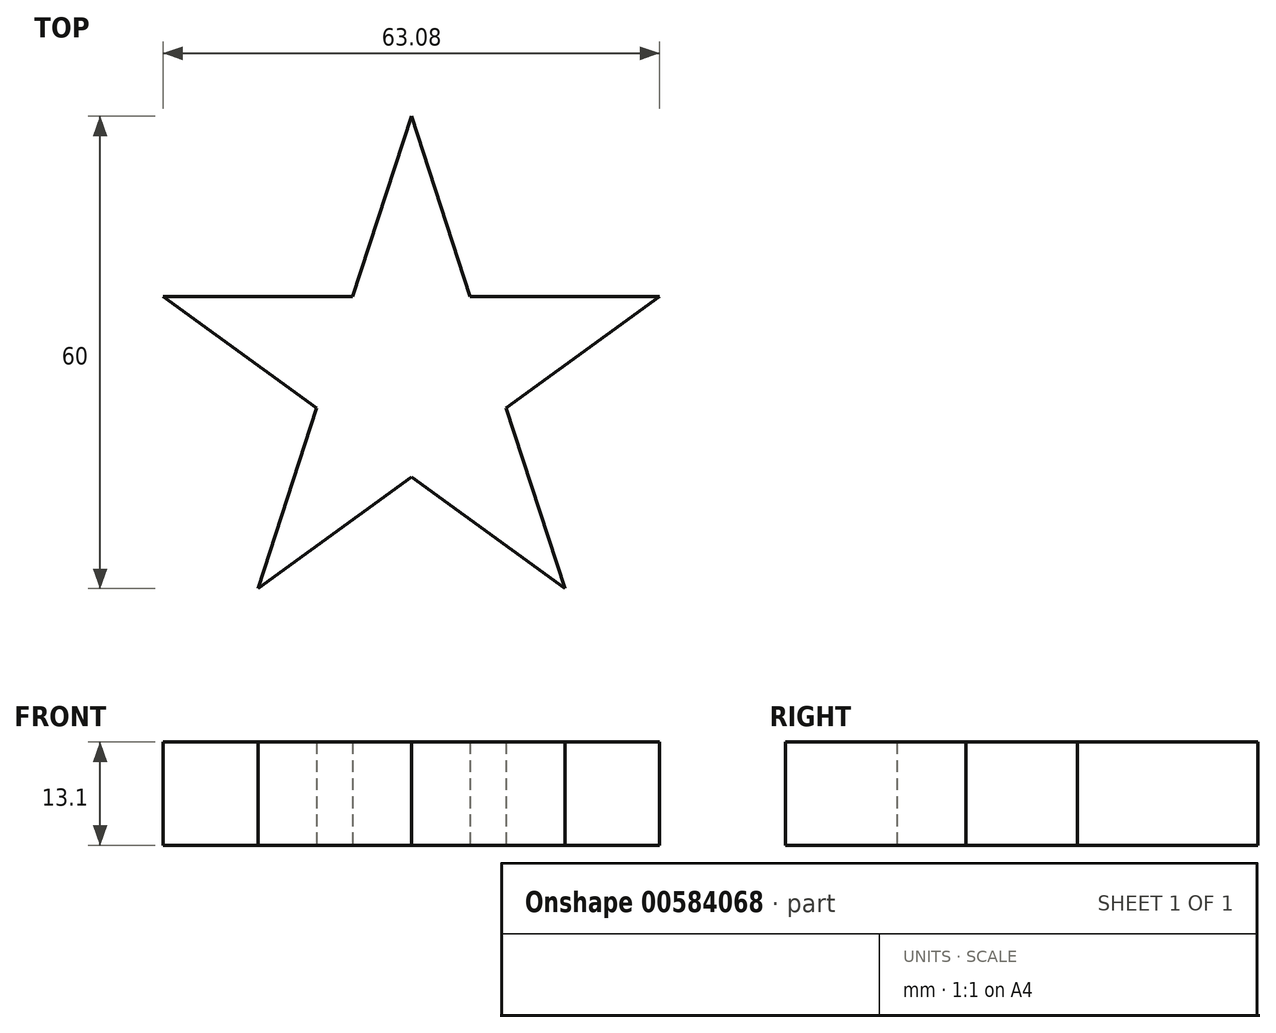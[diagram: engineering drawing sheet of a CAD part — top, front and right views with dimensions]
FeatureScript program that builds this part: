
annotation { "Feature Type Name" : "Feature", "Feature Type Description" : "" }
export const myFeature = defineFeature(function(context is Context, id is Id, definition is map)
    precondition{}
    {
        {
            var Q0;
            Q0=qCreatedBy(makeId("Top.planeOp"),FACE);
            var sketch = newSketch(context, id + "F0", { "sketchPlane" : qUnion([Q0])});
            skLineSegment(sketch, "E0.MirrorCS", {"start": v(12.05, -39.93) * mm, "end": v(7.45, -25.76) * mm, "construction": true});
            skLineSegment(sketch, "E1.MirrorCS", {"start": v(7.45, -25.76) * mm, "end": v(-7.45, -25.76) * mm, "construction": true});
            skLineSegment(sketch, "E2.MirrorCS", {"start": v(-12.05, -39.93) * mm, "end": v(-19.5, -62.85) * mm});
            skLineSegment(sketch, "E3.MirrorCS", {"start": v(-7.45, -25.76) * mm, "end": v(0, -2.85) * mm});
            skLineSegment(sketch, "E4.MirrorCS", {"start": v(31.54, -25.76) * mm, "end": v(7.45, -25.76) * mm});
            skLineSegment(sketch, "E5.MirrorCS", {"start": v(12.05, -39.93) * mm, "end": v(31.54, -25.76) * mm});
            skLineSegment(sketch, "E6.MirrorCS", {"start": v(12.05, -39.93) * mm, "end": v(19.5, -62.85) * mm});
            skLineSegment(sketch, "E7.MirrorCS", {"start": v(19.5, -62.85) * mm, "end": v(0, -48.68) * mm});
            skLineSegment(sketch, "E8.MirrorCS", {"start": v(-31.54, -25.76) * mm, "end": v(-12.05, -39.93) * mm});
            skLineSegment(sketch, "E9.MirrorCS", {"start": v(-7.45, -25.76) * mm, "end": v(-31.54, -25.76) * mm});
            skPoint(sketch, "E10.MirrorP", {"position": v(0, -36.01) * mm});
            skLineSegment(sketch, "E11.MirrorCS", {"start": v(0, -2.85) * mm, "end": v(7.45, -25.76) * mm});
            skLineSegment(sketch, "E12.MirrorCS", {"start": v(-7.45, -25.76) * mm, "end": v(-12.05, -39.93) * mm, "construction": true});
            skLineSegment(sketch, "E13.MirrorCS", {"start": v(-19.5, -62.85) * mm, "end": v(0, -48.68) * mm});
            skLineSegment(sketch, "E14.MirrorCS", {"start": v(-12.05, -39.93) * mm, "end": v(0, -48.68) * mm, "construction": true});
            skLineSegment(sketch, "E15.MirrorCS", {"start": v(0, -48.68) * mm, "end": v(12.05, -39.93) * mm, "construction": true});
            skPoint(sketch, "E16.MirrorP", {"position": v(9.75, -32.85) * mm});
            skSolve(sketch);
        }
        {
            var Q0;
            Q0=makeQuery(id+"F0.imprint","IMPRINT",FACE,{"disambiguationData":[TD([[makeQuery(id+"F0.imprint","IMPRINT",EDGE,{"derivedFrom":sQuery(id+"F0.wireOp",EDGE,"E2.MirrorCS")}),1.0]])]});
            extrude(context, id + "F1", {"entities" : qUnion([Q0]), "depth" : .4 * mm});
        }
        {
            var Q0;
            Q0=makeQuery(id+"F1.opExtrude","CAP_FACE",FACE,{"disambiguationData":[OSD([sQuery(id+"F0.wireOp",EDGE,"E2.MirrorCS"),sQuery(id+"F0.wireOp",EDGE,"E3.MirrorCS"),sQuery(id+"F0.wireOp",EDGE,"E4.MirrorCS"),sQuery(id+"F0.wireOp",EDGE,"E5.MirrorCS"),sQuery(id+"F0.wireOp",EDGE,"E6.MirrorCS"),sQuery(id+"F0.wireOp",EDGE,"E7.MirrorCS"),sQuery(id+"F0.wireOp",EDGE,"E8.MirrorCS"),sQuery(id+"F0.wireOp",EDGE,"E9.MirrorCS"),sQuery(id+"F0.wireOp",EDGE,"E11.MirrorCS"),sQuery(id+"F0.wireOp",EDGE,"E13.MirrorCS")])],"isStart":false});
            var sketch = newSketch(context, id + "F2", { "sketchPlane" : qUnion([Q0])});
            skLineSegment(sketch, "E17", {"start": v(7.45, -25.76) * mm, "end": v(12.05, -39.93) * mm});
            skLineSegment(sketch, "E18", {"start": v(31.54, -25.76) * mm, "end": v(9.75, -32.85) * mm});
            skPoint(sketch, "E19", {"position": v(15.25, -31.06) * mm});
            skSolve(sketch);
        }
        {
            var Q0;
            Q0=sQuery(id+"F2.wireOp",EDGE,"E18");
            cPlane(context, id + "F3", {"entities" : qUnion([Q0]), "cplaneType" : CPlaneType.LINE_ANGLE, "offset" : 25 * mm, "angle" : 0 * degree, "width" : 150 * mm, "height" : 150 * mm});
        }
        {
            var Q0;
            Q0=qCreatedBy(id+"F3.planeOp",FACE);
            var sketch = newSketch(context, id + "F4", { "sketchPlane" : qUnion([Q0])});
            skLineSegment(sketch, "E20", {"start": v(4.9, 0.4) * mm, "end": v(5.9, 0.4) * mm});
            skArc(sketch, "E21", {"start": v(5.9, 0.4) * mm, "mid": v(5.61, 1.1) * mm, "end": v(4.9, 1.4) * mm});
            skLineSegment(sketch, "E22", {"start": v(4.9, 0.4) * mm, "end": v(4.9, 1.4) * mm});
            skSolve(sketch);
        }
        {
            var Q0;
            Q0=makeQuery(id+"F2.imprint","IMPRINT",FACE,{"disambiguationData":[TD([[makeQuery(id+"F2.imprint","IMPRINT",EDGE,{"derivedFrom":makeQuery(id+"F1.opExtrude","CAP_EDGE",EDGE,{"disambiguationData":[OSD([sQuery(id+"F0.wireOp",EDGE,"E2.MirrorCS")])],"isStart":false})}),1.0]])]});
            var Q1;
            {var subQ2=sQuery(id+"F2.wireOp",EDGE,"E18");Q1=makeQuery(id+"F2.imprint","IMPRINT",FACE,{"disambiguationData":[TD([[makeQuery(id+"F2.imprint","IMPRINT",EDGE,{"derivedFrom":subQ2}),1.0]])]});}
            extrude(context, id + "F5", {"entities" : qUnion([Q0, Q1]), "operationType" : NewBodyOperationType.ADD, "depth" : 12.7 * mm, "offsetDistance" : 25 * mm});
        }
        {
            var Q0;
            Q0=makeQuery(id+"F1.opExtrude","CAP_FACE",FACE,{"disambiguationData":[OSD([sQuery(id+"F0.wireOp",EDGE,"E2.MirrorCS"),sQuery(id+"F0.wireOp",EDGE,"E3.MirrorCS"),sQuery(id+"F0.wireOp",EDGE,"E4.MirrorCS"),sQuery(id+"F0.wireOp",EDGE,"E5.MirrorCS"),sQuery(id+"F0.wireOp",EDGE,"E6.MirrorCS"),sQuery(id+"F0.wireOp",EDGE,"E7.MirrorCS"),sQuery(id+"F0.wireOp",EDGE,"E8.MirrorCS"),sQuery(id+"F0.wireOp",EDGE,"E9.MirrorCS"),sQuery(id+"F0.wireOp",EDGE,"E11.MirrorCS"),sQuery(id+"F0.wireOp",EDGE,"E13.MirrorCS")])],"isStart":false});
            extrude(context, id + "F6", {"entities" : qUnion([Q0]), "operationType" : NewBodyOperationType.ADD, "depth" : 12.7 * mm, "offsetDistance" : 25 * mm});
        }
    });
